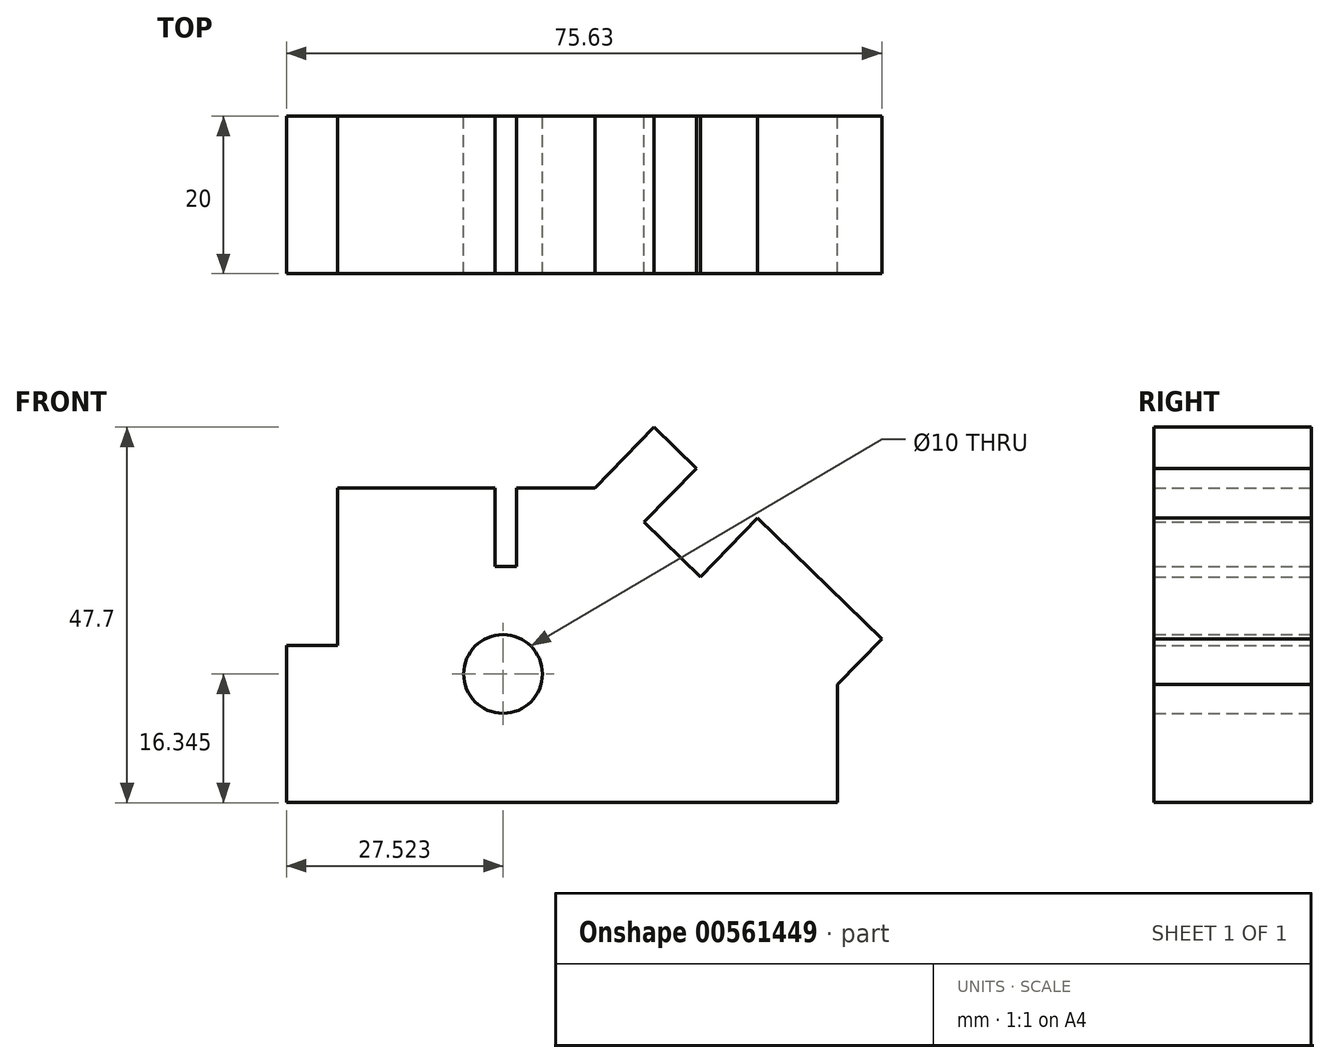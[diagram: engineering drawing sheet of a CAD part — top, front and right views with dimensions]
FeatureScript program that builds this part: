
annotation { "Feature Type Name" : "Feature", "Feature Type Description" : "" }
export const myFeature = defineFeature(function(context is Context, id is Id, definition is map)
    precondition{}
    {
        {
            var Q0;
            Q0=qCreatedBy(makeId("Front.planeOp"),FACE);
            var sketch = newSketch(context, id + "F0", { "sketchPlane" : qUnion([Q0])});
            skLineSegment(sketch, "E0", {"start": v(-40.2, 31.15) * mm, "end": v(-20.2, 31.15) * mm});
            skLineSegment(sketch, "E1", {"start": v(-20.2, 31.15) * mm, "end": v(-20.2, 21.15) * mm});
            skLineSegment(sketch, "E2", {"start": v(-20.2, 21.15) * mm, "end": v(-17.5, 21.15) * mm});
            skLineSegment(sketch, "E3", {"start": v(-17.5, 21.15) * mm, "end": v(-17.5, 31.15) * mm});
            skLineSegment(sketch, "E4", {"start": v(-17.5, 31.15) * mm, "end": v(-7.5, 31.15) * mm});
            skLineSegment(sketch, "E5", {"start": v(-7.5, 31.15) * mm, "end": v(0, 38.85) * mm});
            skLineSegment(sketch, "E6", {"start": v(0, 38.85) * mm, "end": v(5.35, 33.63) * mm});
            skLineSegment(sketch, "E7", {"start": v(5.35, 33.63) * mm, "end": v(-1.27, 26.83) * mm});
            skLineSegment(sketch, "E8", {"start": v(-1.27, 26.83) * mm, "end": v(5.9, 19.85) * mm});
            skLineSegment(sketch, "E9", {"start": v(5.9, 19.85) * mm, "end": v(13.14, 27.29) * mm});
            skLineSegment(sketch, "E10", {"start": v(13.14, 27.29) * mm, "end": v(28.9, 11.93) * mm});
            skLineSegment(sketch, "E11", {"start": v(28.9, 11.93) * mm, "end": v(23.27, 6.15) * mm});
            skLineSegment(sketch, "E12", {"start": v(23.27, 6.15) * mm, "end": v(23.27, -8.85) * mm});
            skLineSegment(sketch, "E13", {"start": v(-40.2, 31.15) * mm, "end": v(-40.2, 11.15) * mm});
            skLineSegment(sketch, "E14", {"start": v(-40.2, 11.15) * mm, "end": v(-46.73, 11.15) * mm});
            skLineSegment(sketch, "E15", {"start": v(-46.73, 11.15) * mm, "end": v(-46.73, -8.85) * mm});
            skLineSegment(sketch, "E16", {"start": v(-46.73, -8.85) * mm, "end": v(23.27, -8.85) * mm});
            skCircle(sketch, "E17", {"center": v(-19.2, 7.5) * mm, "radius": 5 * mm});
            skSolve(sketch);
        }
        {
            var Q0;
            Q0 = qSketchRegion(id + "F0", true);
            extrude(context, id + "F1", {"entities" : qUnion([Q0]), "depth" : 20 * mm, "offsetDistance" : 25 * mm});
        }
    });
